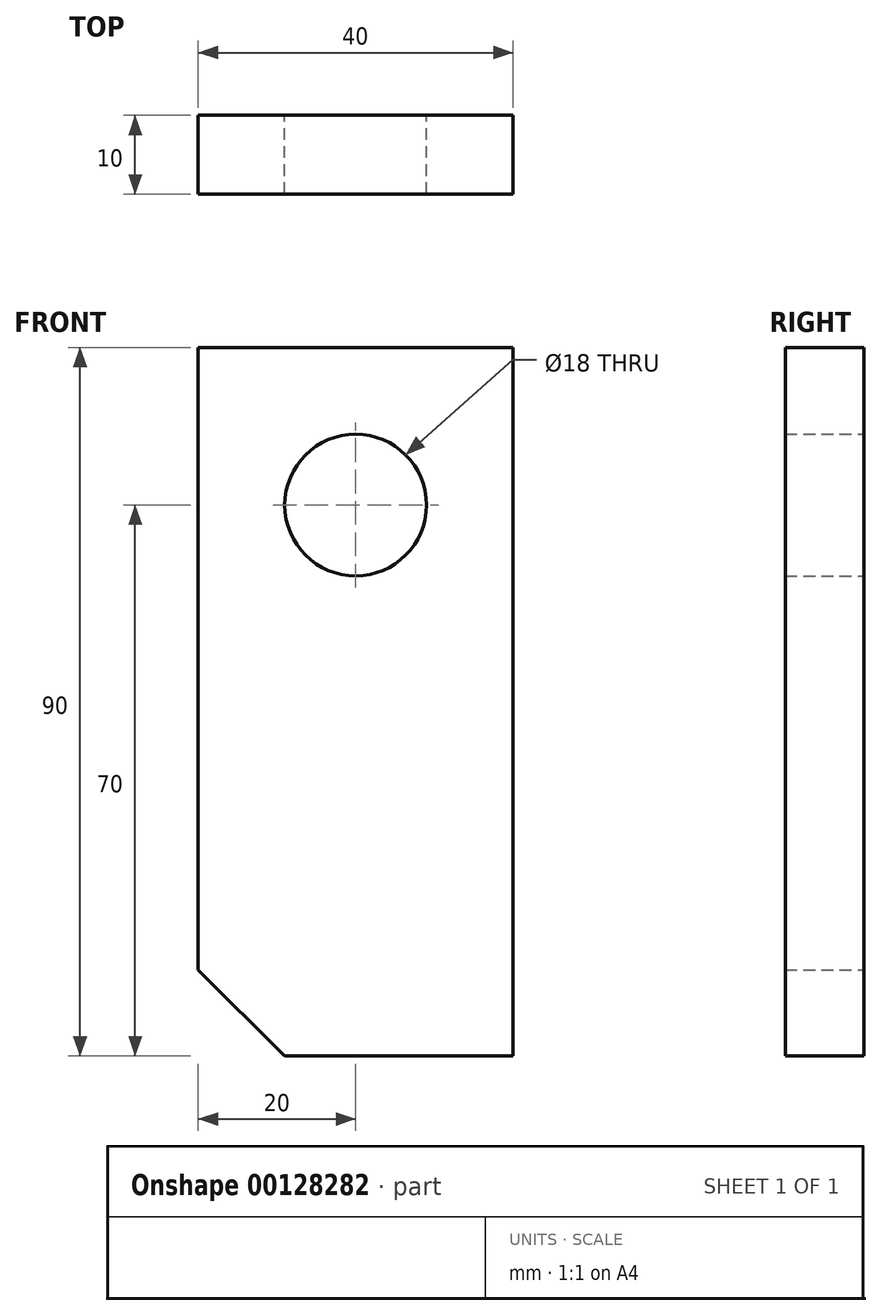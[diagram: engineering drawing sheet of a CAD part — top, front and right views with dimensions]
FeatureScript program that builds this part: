
annotation { "Feature Type Name" : "Feature", "Feature Type Description" : "" }
export const myFeature = defineFeature(function(context is Context, id is Id, definition is map)
    precondition{}
    {
        {
            var Q0;
            Q0=qCreatedBy(makeId("Front.planeOp"),FACE);
            cPlane(context, id + "F0", {"entities" : qUnion([Q0]), "cplaneType" : CPlaneType.OFFSET, "offset" : 1 * mm, "width" : 150 * mm, "height" : 150 * mm});
        }
        {
            var Q0;
            Q0=qCreatedBy(id+"F0.planeOp",FACE);
            var sketch = newSketch(context, id + "F1", { "sketchPlane" : qUnion([Q0])});
            skCircle(sketch, "E0", {"center": v(0, 0) * mm, "radius": 9 * mm});
            skLineSegment(sketch, "E1", {"start": v(20, 20) * mm, "end": v(-20, 20) * mm});
            skLineSegment(sketch, "E2", {"start": v(-20, 20) * mm, "end": v(-20, -59.04) * mm});
            skLineSegment(sketch, "E3", {"start": v(-9.04, -70) * mm, "end": v(20, -70) * mm});
            skLineSegment(sketch, "E4", {"start": v(20, -70) * mm, "end": v(20, 20) * mm});
            skLineSegment(sketch, "E5", {"start": v(-20, -59.04) * mm, "end": v(-9.04, -70) * mm});
            skSolve(sketch);
        }
        {
            var Q0;
            Q0 = qSketchRegion(id + "F1", true);
            extrude(context, id + "F2", {"entities" : qUnion([Q0]), "depth" : 10 * mm});
        }
    });
